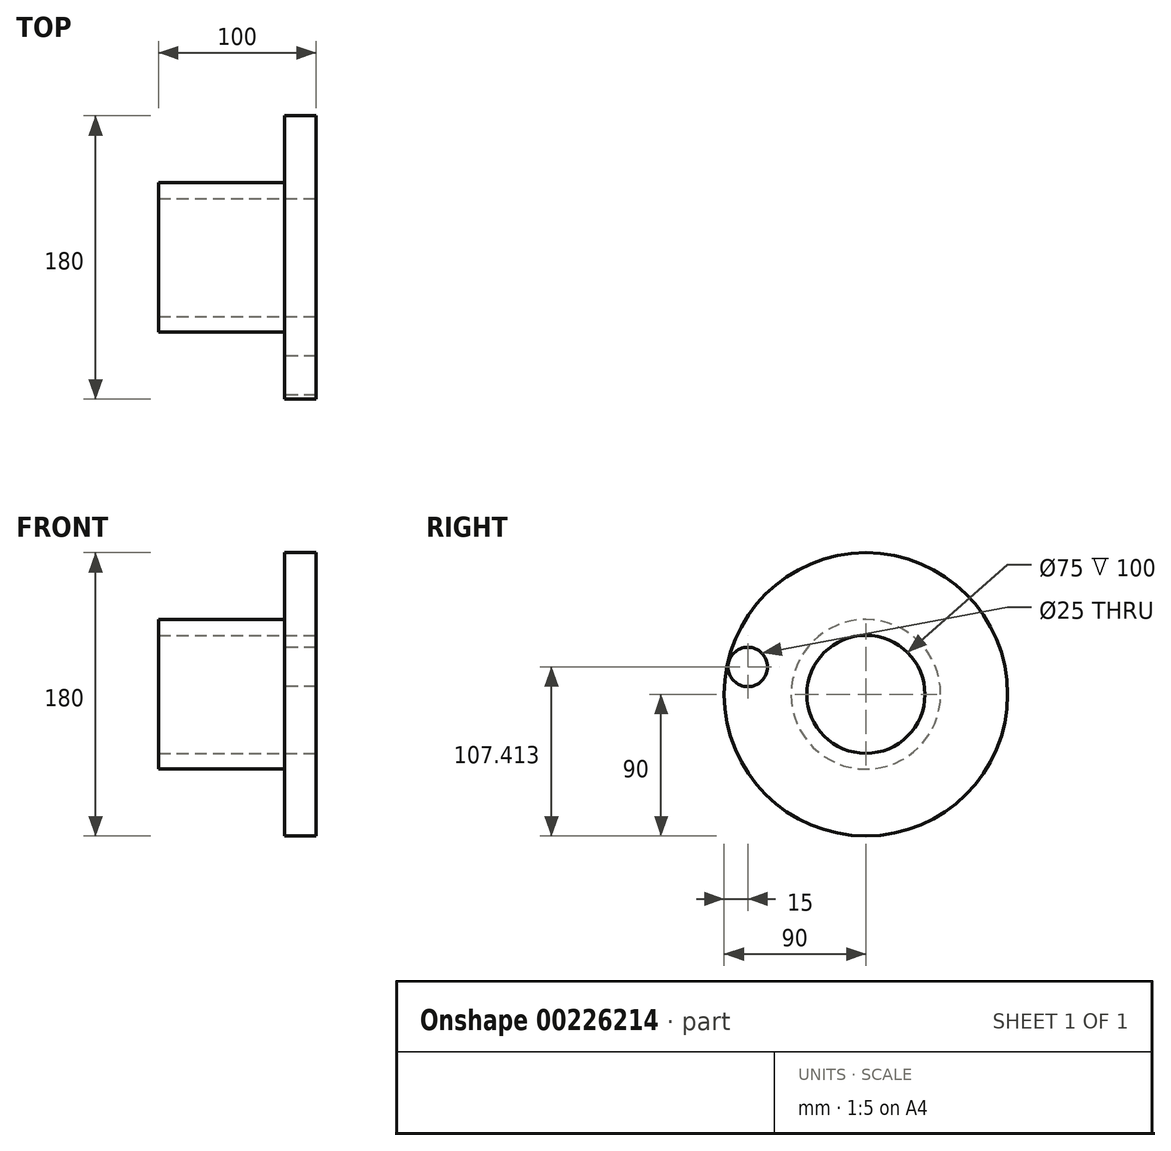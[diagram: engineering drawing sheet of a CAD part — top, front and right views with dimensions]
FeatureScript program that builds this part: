
annotation { "Feature Type Name" : "Feature", "Feature Type Description" : "" }
export const myFeature = defineFeature(function(context is Context, id is Id, definition is map)
    precondition{}
    {
        {
            var Q0;
            Q0=qCreatedBy(makeId("Front.planeOp"),FACE);
            var sketch = newSketch(context, id + "F0", { "sketchPlane" : qUnion([Q0])});
            skLineSegment(sketch, "E0", {"start": v(0, 0) * mm, "end": v(-161.01, 0) * mm, "construction": true});
            skLineSegment(sketch, "E1.bottom", {"start": v(-53.19, 90) * mm, "end": v(-33.19, 90) * mm});
            skLineSegment(sketch, "E1.top", {"start": v(-133.19, 37.5) * mm, "end": v(-33.19, 37.5) * mm});
            skLineSegment(sketch, "E1.left", {"start": v(-133.19, 47.5) * mm, "end": v(-133.19, 37.5) * mm});
            skLineSegment(sketch, "E1.right", {"start": v(-33.19, 90) * mm, "end": v(-33.19, 37.5) * mm});
            skLineSegment(sketch, "E2.top", {"start": v(-133.19, 47.5) * mm, "end": v(-53.19, 47.5) * mm});
            skLineSegment(sketch, "E2.right", {"start": v(-53.19, 90) * mm, "end": v(-53.19, 47.5) * mm});
            skSolve(sketch);
        }
        {
            var Q0;
            Q0=makeQuery(id+"F0.imprint","IMPRINT",FACE,{"disambiguationData":[TD([[makeQuery(id+"F0.imprint","IMPRINT",EDGE,{"derivedFrom":sQuery(id+"F0.wireOp",EDGE,"E1.bottom")}),-1.0]])]});
            var Q1;
            Q1=sQuery(id+"F0.wireOp",EDGE,"E0");
            revolve(context, id + "F1", {"entities" : qUnion([Q0]), "axis" : qUnion([Q1]), "revolveType" : RevolveType.FULL});
        }
        {
            var Q0;
            Q0=makeQuery(id+"F1.opRevolve","SWEPT_FACE",FACE,{"disambiguationData":[OSD([sQuery(id+"F0.wireOp",EDGE,"E2.right")])]});
            var sketch = newSketch(context, id + "F2", { "sketchPlane" : qUnion([Q0])});
            skCircle(sketch, "E3", {"center": v(75, 17.41) * mm, "radius": 12.5 * mm});
            skSolve(sketch);
        }
        {
            var Q0;
            Q0 = qSketchRegion(id + "F2", true);
            extrude(context, id + "F3", {"entities" : qUnion([Q0]), "operationType" : NewBodyOperationType.REMOVE, "endBound" : BoundingType.THROUGH_ALL, "oppositeDirection" : true, "depth" : 25 * mm});
        }
    });
